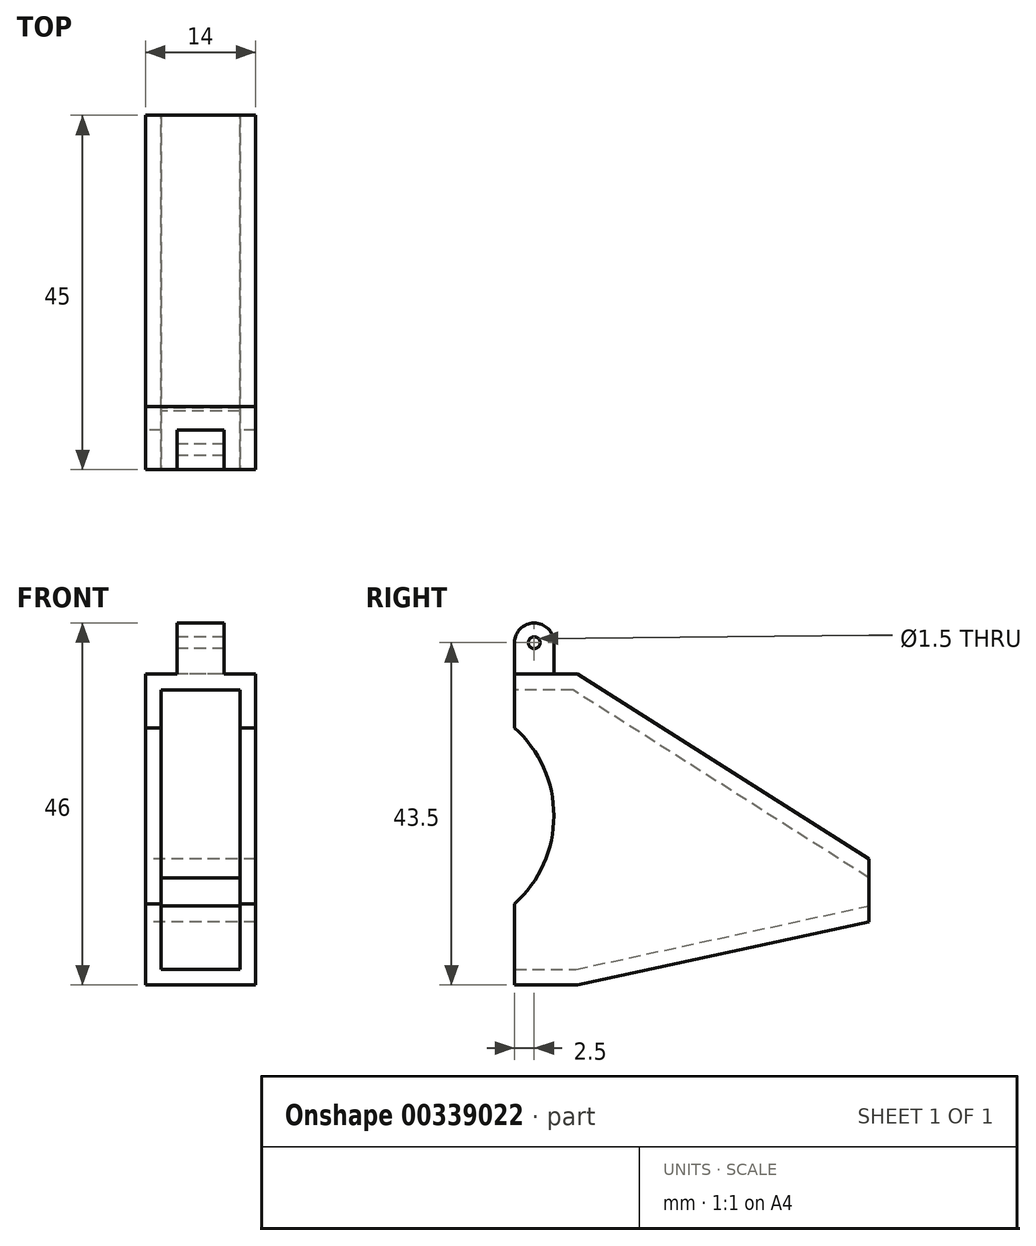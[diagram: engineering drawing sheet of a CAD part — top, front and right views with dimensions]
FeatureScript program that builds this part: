
annotation { "Feature Type Name" : "Feature", "Feature Type Description" : "" }
export const myFeature = defineFeature(function(context is Context, id is Id, definition is map)
    precondition{}
    {
        {
            var Q0;
            Q0=qCreatedBy(makeId("Right.planeOp"),FACE);
            var sketch = newSketch(context, id + "F0", { "sketchPlane" : qUnion([Q0])});
            skLineSegment(sketch, "E0", {"start": v(45, 16) * mm, "end": v(8, 39.5) * mm});
            skLineSegment(sketch, "E1", {"start": v(8, 39.5) * mm, "end": v(0, 39.5) * mm});
            skLineSegment(sketch, "E2", {"start": v(0, 39.5) * mm, "end": v(0, 32.68) * mm});
            skLineSegment(sketch, "E3", {"start": v(0, 0) * mm, "end": v(0, 10.32) * mm});
            skArc(sketch, "E4", {"start": v(0, 32.68) * mm, "mid": v(5, 21.5) * mm, "end": v(0, 10.32) * mm});
            skLineSegment(sketch, "E5", {"start": v(0, 0) * mm, "end": v(8, 0) * mm});
            skLineSegment(sketch, "E6", {"start": v(8, 0) * mm, "end": v(45, 8) * mm});
            skLineSegment(sketch, "E7", {"start": v(45, 16) * mm, "end": v(45, 8) * mm});
            skSolve(sketch);
        }
        {
            var Q0;
            Q0 = qSketchRegion(id + "F0", true);
            extrude(context, id + "F1", {"entities" : qUnion([Q0]), "endBound" : BoundingType.SYMMETRIC, "depth" : 14 * mm});
        }
        {
            var Q0;
            Q0=makeQuery(id+"F1.opExtrude","SWEPT_FACE",FACE,{"disambiguationData":[OSD([sQuery(id+"F0.wireOp",EDGE,"E2")])]});
            var Q1;
            Q1=makeQuery(id+"F1.opExtrude","SWEPT_FACE",FACE,{"disambiguationData":[OSD([sQuery(id+"F0.wireOp",EDGE,"E4")])]});
            var Q2;
            Q2=makeQuery(id+"F1.opExtrude","SWEPT_FACE",FACE,{"disambiguationData":[OSD([sQuery(id+"F0.wireOp",EDGE,"E3")])]});
            var Q3;
            Q3=makeQuery(id+"F1.opExtrude","SWEPT_FACE",FACE,{"disambiguationData":[OSD([sQuery(id+"F0.wireOp",EDGE,"IZ5NJi5X-YBgm-ARmo-nhE6-vQBoKQWzUZJj")])]});
            var Q4;
            Q4=makeQuery(id+"F1.opExtrude","SWEPT_FACE",FACE,{"disambiguationData":[OSD([sQuery(id+"F0.wireOp",EDGE,"E7")])]});
            shell(context, id + "F2", {"entities" : qUnion([Q0, Q1, Q2, Q3, Q4]), "thickness" : 2 * mm});
        }
        {
            var Q0;
            Q0=qCreatedBy(makeId("Right.planeOp"),FACE);
            var sketch = newSketch(context, id + "F3", { "sketchPlane" : qUnion([Q0])});
            skLineSegment(sketch, "E8.0", {"start": v(8, 39.5) * mm, "end": v(0, 39.5) * mm});
            skLineSegment(sketch, "E9", {"start": v(0, 39.5) * mm, "end": v(0, 43.5) * mm});
            skLineSegment(sketch, "E10", {"start": v(0, 43.5) * mm, "end": v(5, 43.5) * mm, "construction": true});
            skLineSegment(sketch, "E11", {"start": v(5, 43.5) * mm, "end": v(5, 39.5) * mm});
            skArc(sketch, "E12", {"start": v(0, 43.5) * mm, "mid": v(2.5, 46) * mm, "end": v(5, 43.5) * mm});
            skCircle(sketch, "E13", {"center": v(2.5, 43.5) * mm, "radius": 0.75 * mm});
            skSolve(sketch);
        }
        {
            var Q0;
            {var subQ1=sQuery(id+"F3.wireOp",EDGE,"E9");Q0=makeQuery(id+"F3.imprint","IMPRINT",FACE,{"disambiguationData":[TD([[makeQuery(id+"F3.imprint","IMPRINT",EDGE,{"derivedFrom":subQ1}),-1.0]])]});}
            extrude(context, id + "F4", {"entities" : qUnion([Q0]), "operationType" : NewBodyOperationType.ADD, "endBound" : BoundingType.SYMMETRIC, "depth" : 6 * mm});
        }
    });
